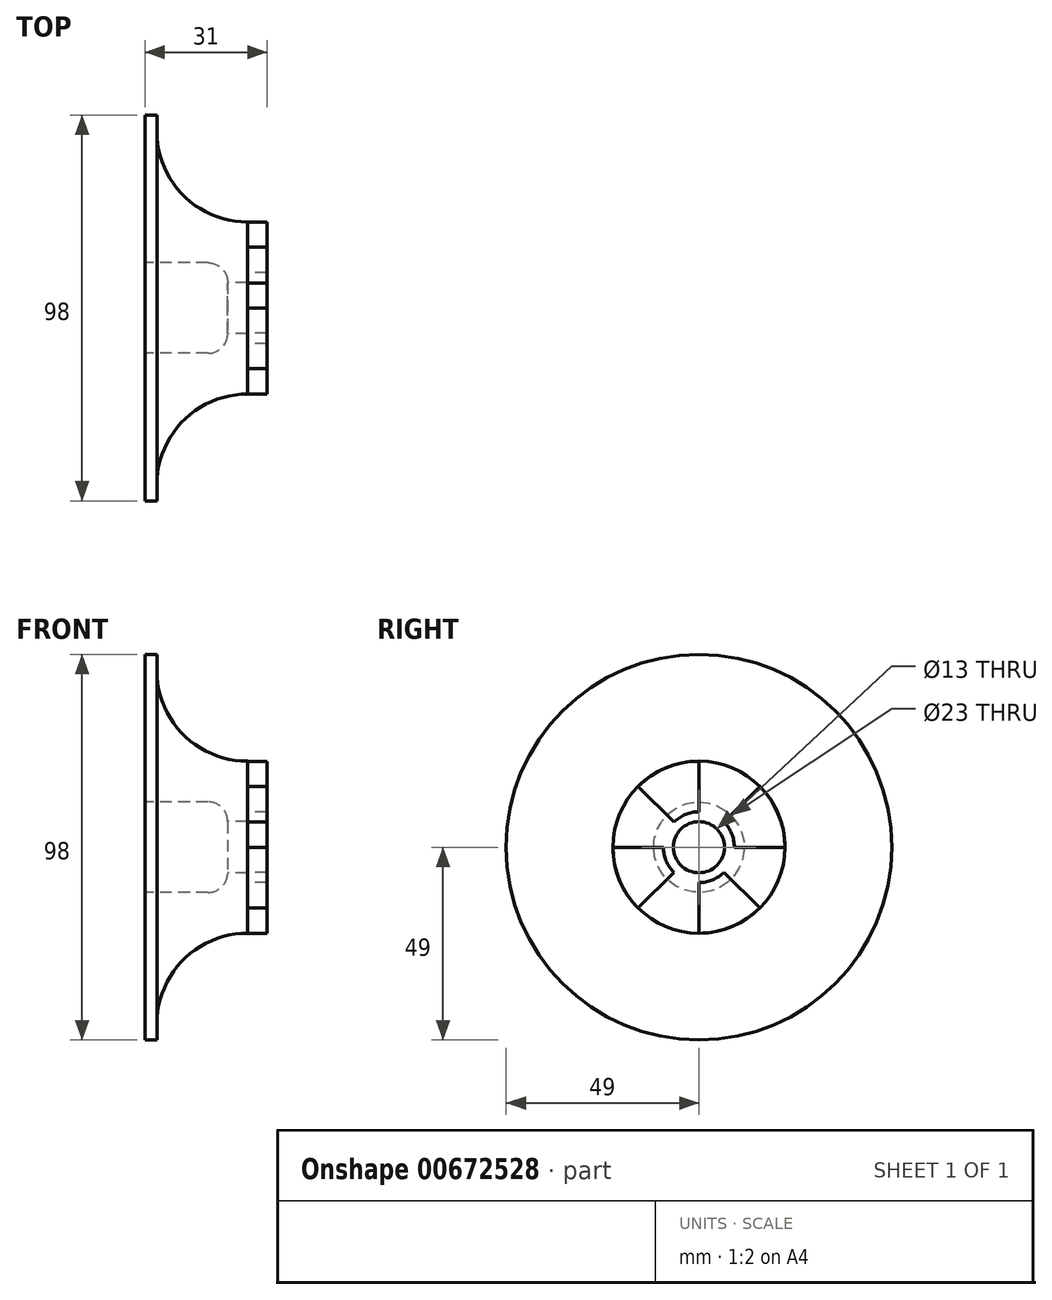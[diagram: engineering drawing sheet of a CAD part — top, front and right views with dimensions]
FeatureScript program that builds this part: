
annotation { "Feature Type Name" : "Feature", "Feature Type Description" : "" }
export const myFeature = defineFeature(function(context is Context, id is Id, definition is map)
    precondition{}
    {
        {
            var Q0;
            Q0=qCreatedBy(makeId("Top.planeOp"),FACE);
            var sketch = newSketch(context, id + "F0", { "sketchPlane" : qUnion([Q0])});
            skLineSegment(sketch, "E0", {"start": v(0, 0) * mm, "end": v(0, -9) * mm, "construction": true});
            skLineSegment(sketch, "E1", {"start": v(0, -9) * mm, "end": v(-31, -9) * mm});
            skLineSegment(sketch, "E2", {"start": v(-31, -9) * mm, "end": v(-31, -6.5) * mm});
            skLineSegment(sketch, "E3", {"start": v(-31, -6.5) * mm, "end": v(-36, -6.5) * mm});
            skLineSegment(sketch, "E4", {"start": v(-36, -6.5) * mm, "end": v(-36, -11.5) * mm});
            skLineSegment(sketch, "E5", {"start": v(0, -9) * mm, "end": v(0, -49) * mm});
            skLineSegment(sketch, "E6", {"start": v(0, -49) * mm, "end": v(-3, -49) * mm});
            skLineSegment(sketch, "E7", {"start": v(-3, -49) * mm, "end": v(-3, -44.85) * mm});
            skArc(sketch, "E8.filletArc", {"start": v(-3, -44.85) * mm, "mid": v(-9.74, -28.6) * mm, "end": v(-26, -21.85) * mm});
            skLineSegment(sketch, "E9", {"start": v(-36, -11.5) * mm, "end": v(-57, -11.5) * mm});
            skLineSegment(sketch, "E10", {"start": v(0, 0) * mm, "end": v(15.04, 0) * mm, "construction": true});
            skLineSegment(sketch, "E11", {"start": v(-28.5, -21.85) * mm, "end": v(-28.5, -32.8) * mm, "construction": true});
            skArc(sketch, "E12.MirrorCS", {"start": v(-54, -44.85) * mm, "mid": v(-47.26, -28.6) * mm, "end": v(-31, -21.85) * mm});
            skLineSegment(sketch, "E13.MirrorCS", {"start": v(-57, -49) * mm, "end": v(-54, -49) * mm});
            skLineSegment(sketch, "E14.MirrorCS", {"start": v(-54, -49) * mm, "end": v(-54, -44.85) * mm});
            skLineSegment(sketch, "E15", {"start": v(-57, -49) * mm, "end": v(-57, -11.5) * mm});
            skLineSegment(sketch, "E16", {"start": v(-31, -21.85) * mm, "end": v(-26, -21.85) * mm});
            skSolve(sketch);
        }
        {
            var Q0;
            Q0=makeQuery(id+"F0.imprint","IMPRINT",FACE,{"disambiguationData":[TD([[makeQuery(id+"F0.imprint","IMPRINT",EDGE,{"derivedFrom":sQuery(id+"F0.wireOp",EDGE,"E1")}),1.0]])]});
            var Q1;
            Q1=sQuery(id+"F0.wireOp",EDGE,"E10");
            revolve(context, id + "F1", {"entities" : qUnion([Q0]), "axis" : qUnion([Q1]), "revolveType" : RevolveType.FULL});
        }
        {
            var Q0;
            Q0=makeQuery(id+"F1.opRevolve","SWEPT_EDGE",EDGE,{"disambiguationData":[OSD([sQuery(id+"F0.wireOp",EDGE,"c69ddd43-5696-4591-9470-7416ab7c15ab0.MirrorCS"),sQuery(id+"F0.wireOp",EDGE,"d127276e-ed42-4071-8a29-d4c84e1c8a1b0.MirrorCS")])]});
            var Q1;
            Q1=makeQuery(id+"F1.opRevolve","SWEPT_EDGE",EDGE,{"disambiguationData":[OSD([sQuery(id+"F0.wireOp",EDGE,"E6"),sQuery(id+"F0.wireOp",EDGE,"E7")])]});
            fillet(context, id + "F2", {"entities" : qUnion([Q0, Q1]), "radius" : 5 * mm, "tangentPropagation" : true, "allowEdgeOverflow" : false});
        }
        {
            var Q0;
            Q0=makeQuery(id+"F1.opRevolve","SWEPT_FACE",FACE,{"disambiguationData":[OSD([sQuery(id+"F0.wireOp",EDGE,"E2")])]});
            var sketch = newSketch(context, id + "F3", { "sketchPlane" : qUnion([Q0])});
            skCircle(sketch, "E17", {"center": v(0, 0) * mm, "radius": 78.83 * mm});
            skSolve(sketch);
        }
        {
            var Q0;
            Q0 = qSketchRegion(id + "F3", true);
            extrude(context, id + "F4", {"entities" : qUnion([Q0]), "operationType" : NewBodyOperationType.REMOVE, "depth" : 40 * mm, "offsetDistance" : 25 * mm});
        }
        {
            var Q0;
            Q0=makeQuery(id+"F4.boolean.opBoolean","MERGE",FACE,{"derivedFrom":[makeQuery(id+"F1.opRevolve","SWEPT_FACE",FACE,{"disambiguationData":[OSD([sQuery(id+"F0.wireOp",EDGE,"E2")])]}),makeQuery(id+"F4.opExtrude","CAP_FACE",FACE,{"disambiguationData":[OSD([sQuery(id+"F3.wireOp",EDGE,"E17")])],"isStart":true})]});
            var sketch = newSketch(context, id + "F5", { "sketchPlane" : qUnion([Q0])});
            skCircle(sketch, "E18", {"center": v(0, 0) * mm, "radius": 21.85 * mm});
            skCircle(sketch, "E19", {"center": v(0, 0) * mm, "radius": 9 * mm});
            skLineSegment(sketch, "E20", {"start": v(6.36, 6.36) * mm, "end": v(15.45, 15.45) * mm});
            skLineSegment(sketch, "E21", {"start": v(-6.36, 6.36) * mm, "end": v(-15.45, 15.45) * mm});
            skLineSegment(sketch, "E22", {"start": v(0, 9) * mm, "end": v(0, 21.85) * mm});
            skLineSegment(sketch, "E23", {"start": v(-21.85, 0) * mm, "end": v(-21.85, 0) * mm});
            skLineSegment(sketch, "E24", {"start": v(-6.36, -6.36) * mm, "end": v(-15.45, -15.45) * mm});
            skLineSegment(sketch, "E25", {"start": v(0, -9) * mm, "end": v(0, -21.85) * mm});
            skLineSegment(sketch, "E26", {"start": v(6.36, -6.36) * mm, "end": v(15.45, -15.45) * mm});
            skLineSegment(sketch, "E27", {"start": v(6.5, 0) * mm, "end": v(21.85, 0) * mm});
            skLineSegment(sketch, "E28", {"start": v(-9, 0) * mm, "end": v(-21.85, 0) * mm});
            skSolve(sketch);
        }
        {
            var Q0;
            {var subQ0=sQuery(id+"F5.wireOp",EDGE,"E20");Q0=makeQuery(id+"F5.imprint","IMPRINT",FACE,{"disambiguationData":[TD([[makeQuery(id+"F5.imprint","IMPRINT",EDGE,{"derivedFrom":subQ0}),-1.0]])]});}
            var Q1;
            {var subQ0=sQuery(id+"F5.wireOp",EDGE,"E22");Q1=makeQuery(id+"F5.imprint","IMPRINT",FACE,{"disambiguationData":[TD([[makeQuery(id+"F5.imprint","IMPRINT",EDGE,{"derivedFrom":subQ0}),1.0]])]});}
            var Q2;
            {var subQ0=sQuery(id+"F5.wireOp",EDGE,"t8wlPJVO-gki7-LTMt-G8yy-ibpICR7pLRq8");Q2=makeQuery(id+"F5.imprint","IMPRINT",FACE,{"disambiguationData":[TD([[makeQuery(id+"F5.imprint","IMPRINT",EDGE,{"derivedFrom":subQ0}),1.0]])]});}
            var Q3;
            {var subQ0=sQuery(id+"F5.wireOp",EDGE,"E26");Q3=makeQuery(id+"F5.imprint","IMPRINT",FACE,{"disambiguationData":[TD([[makeQuery(id+"F5.imprint","IMPRINT",EDGE,{"derivedFrom":subQ0}),-1.0]])]});}
            var Q4;
            {var subQ0=sQuery(id+"F5.wireOp",EDGE,"E28");Q4=makeQuery(id+"F5.imprint","IMPRINT",FACE,{"disambiguationData":[TD([[makeQuery(id+"F5.imprint","IMPRINT",EDGE,{"derivedFrom":subQ0}),1.0]])]});}
            extrude(context, id + "F6", {"entities" : qUnion([Q0, Q1, Q2, Q3, Q4]), "operationType" : NewBodyOperationType.ADD, "depth" : 5 * mm, "offsetDistance" : 25 * mm});
        }
        {
            var Q0;
            Q0=makeQuery(id+"F1.opRevolve","SWEPT_EDGE",EDGE,{"disambiguationData":[OSD([sQuery(id+"F0.wireOp",EDGE,"E4"),sQuery(id+"F0.wireOp",EDGE,"E9")])]});
            fillet(context, id + "F7", {"entities" : qUnion([Q0]), "radius" : 5 * mm, "tangentPropagation" : true, "allowEdgeOverflow" : false});
        }
    });
